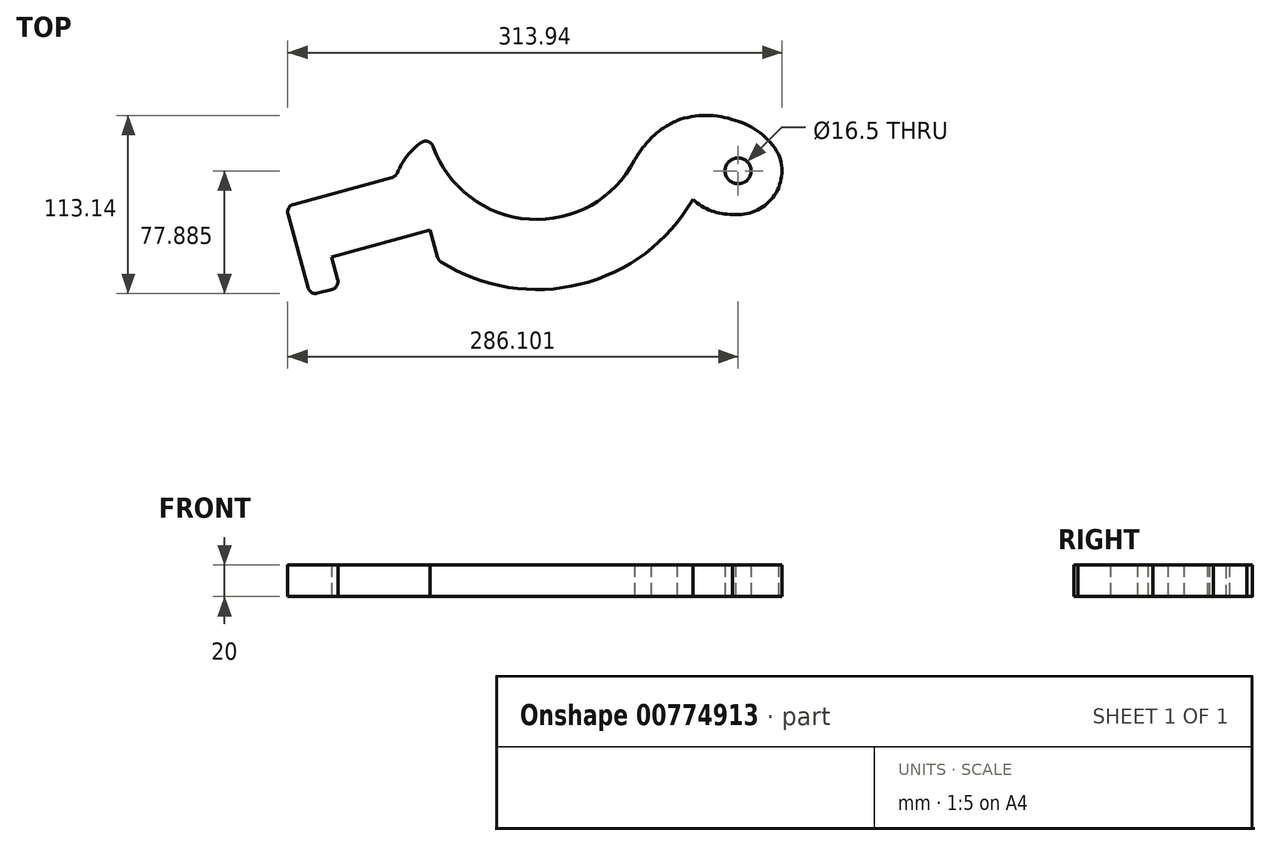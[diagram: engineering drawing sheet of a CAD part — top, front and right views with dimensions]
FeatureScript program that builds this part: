
annotation { "Feature Type Name" : "Feature", "Feature Type Description" : "" }
export const myFeature = defineFeature(function(context is Context, id is Id, definition is map)
    precondition{}
    {
        {
            var Q0;
            Q0=qCreatedBy(makeId("Top.planeOp"),FACE);
            var sketch = newSketch(context, id + "F0", { "sketchPlane" : qUnion([Q0])});
            skArc(sketch, "E0", {"start": v(60.62, -35) * mm, "mid": v(61.37, -33.66) * mm, "end": v(62.1, -32.3) * mm});
            skArc(sketch, "E1", {"start": v(-67.74, -17.64) * mm, "mid": v(-7.86, -69.56) * mm, "end": v(62.1, -32.3) * mm});
            skArc(sketch, "E2.trimOffspring", {"start": v(-67.74, -17.64) * mm, "mid": v(-61.83, -32.8) * mm, "end": v(-52.59, -46.2) * mm});
            skArc(sketch, "E3.trimOffspring", {"start": v(-62.48, -95.92) * mm, "mid": v(26.64, -111.33) * mm, "end": v(99.14, -57.24) * mm});
            skLineSegment(sketch, "E4", {"start": v(0, 0) * mm, "end": v(0, -70) * mm, "construction": true});
            skArc(sketch, "E5", {"start": v(124.4, -66.72) * mm, "mid": v(150.01, -55.92) * mm, "end": v(153.5, -28.33) * mm});
            skCircle(sketch, "E6", {"center": v(127.83, -39.1) * mm, "radius": 8.25 * mm});
            skLineSegment(sketch, "E7", {"start": v(-130.46, -93.7) * mm, "end": v(-67.74, -76.62) * mm});
            skLineSegment(sketch, "E8", {"start": v(-125.2, -113) * mm, "end": v(-130.46, -93.7) * mm});
            skLineSegment(sketch, "E9", {"start": v(0, 0) * mm, "end": v(127.83, -39.1) * mm, "construction": true});
            skLineSegment(sketch, "E10", {"start": v(0, 0) * mm, "end": v(154.45, -47.24) * mm, "construction": true});
            skLineSegment(sketch, "E11", {"start": v(-153.69, -82.63) * mm, "end": v(-144.02, -118.12) * mm});
            skLineSegment(sketch, "E12", {"start": v(-62.48, -95.92) * mm, "end": v(-67.74, -76.62) * mm});
            skLineSegment(sketch, "E13", {"start": v(-67.74, -76.62) * mm, "end": v(-67.74, -76.62) * mm});
            skArc(sketch, "E14", {"start": v(72.58, -18.26) * mm, "mid": v(66.02, -26.21) * mm, "end": v(60.62, -35) * mm});
            skArc(sketch, "E15", {"start": v(89.08, -7.13) * mm, "mid": v(73.45, -17.43) * mm, "end": v(62.1, -32.3) * mm});
            skArc(sketch, "E16.trimOffspring", {"start": v(-62.55, -31.42) * mm, "mid": v(-0.5, -70) * mm, "end": v(62.1, -32.3) * mm, "construction": true});
            skLineSegment(sketch, "E17", {"start": v(-153.69, -82.63) * mm, "end": v(-159.4, -61.64) * mm});
            skLineSegment(sketch, "E18", {"start": v(-125.2, -113) * mm, "end": v(-144.02, -118.12) * mm});
            skLineSegment(sketch, "E19", {"start": v(-159.4, -61.64) * mm, "end": v(-89.46, -42.6) * mm});
            skArc(sketch, "E20", {"start": v(-67.74, -17.64) * mm, "mid": v(-81.03, -28) * mm, "end": v(-89.46, -42.6) * mm});
            skCircle(sketch, "E21", {"center": v(0, 0) * mm, "radius": 70 * mm, "construction": true});
            skArc(sketch, "E22.MirrorCS", {"start": v(102.2, -59.8) * mm, "mid": v(101.55, -59.45) * mm, "end": v(100.9, -59.09) * mm});
            skLineSegment(sketch, "E23", {"start": v(0, 0) * mm, "end": v(0, 88.9) * mm, "construction": true});
            skArc(sketch, "E24", {"start": v(99.14, -57.24) * mm, "mid": v(110.82, -64.52) * mm, "end": v(124.4, -66.72) * mm});
            skArc(sketch, "E25", {"start": v(6.46, 1.5) * mm, "mid": v(7.21, 2.85) * mm, "end": v(7.94, 4.2) * mm});
            skLineSegment(sketch, "E26", {"start": v(-121.9, -40.11) * mm, "end": v(-121.9, -40.11) * mm});
            skArc(sketch, "E27", {"start": v(34.92, 29.38) * mm, "mid": v(34.67, 29.28) * mm, "end": v(34.43, 29.17) * mm});
            skArc(sketch, "E28", {"start": v(70.6, 28.85) * mm, "mid": v(70.6, 28.85) * mm, "end": v(70.6, 28.85) * mm});
            skArc(sketch, "E29", {"start": v(126.08, -7.15) * mm, "mid": v(107.58, -3.84) * mm, "end": v(89.08, -7.13) * mm});
            skArc(sketch, "E30", {"start": v(153.5, -28.33) * mm, "mid": v(141.9, -15) * mm, "end": v(126.08, -7.15) * mm});
            skLineSegment(sketch, "E31", {"start": v(127.83, -39.1) * mm, "end": v(127.83, -30.84) * mm});
            skLineSegment(sketch, "E32", {"start": v(127.83, -39.1) * mm, "end": v(127.83, -47.34) * mm});
            skLineSegment(sketch, "E33", {"start": v(127.83, -39.1) * mm, "end": v(119.58, -39.1) * mm});
            skLineSegment(sketch, "E34", {"start": v(127.83, -39.1) * mm, "end": v(136.08, -39.1) * mm});
            skLineSegment(sketch, "E35", {"start": v(127.83, -39.1) * mm, "end": v(127.83, -47.34) * mm, "construction": true});
            skLineSegment(sketch, "E36", {"start": v(127.83, -128.66) * mm, "end": v(27.83, -128.66) * mm});
            skLineSegment(sketch, "E37", {"start": v(27.83, -128.66) * mm, "end": v(27.83, -118.66) * mm});
            skLineSegment(sketch, "E38", {"start": v(127.83, -128.66) * mm, "end": v(127.83, -118.66) * mm});
            skLineSegment(sketch, "E39.trimOffspring", {"start": v(127.83, -118.66) * mm, "end": v(127.83, -128.66) * mm, "construction": true});
            skLineSegment(sketch, "E40", {"start": v(-130.46, -93.7) * mm, "end": v(127.83, -23.37) * mm, "construction": true});
            skPoint(sketch, "E41.endSnap0", {"position": v(123.7, -39.1) * mm});
            skLineSegment(sketch, "E42", {"start": v(127.83, -39.1) * mm, "end": v(123.84, -24.45) * mm, "construction": true});
            skSolve(sketch);
        }
        {
            var Q0;
            Q0=makeQuery(id+"F0.imprint","IMPRINT",FACE,{"disambiguationData":[TD([[makeQuery(id+"F0.imprint","IMPRINT",EDGE,{"derivedFrom":sQuery(id+"F0.wireOp",EDGE,"E1")}),-1.0]])]});
            extrude(context, id + "F1", {"entities" : qUnion([Q0]), "depth" : 20 * mm, "offsetDistance" : 25 * mm});
        }
        {
            var Q0;
            Q0=makeQuery(id+"F1.opExtrude","SWEPT_EDGE",EDGE,{"disambiguationData":[OSD([sQuery(id+"F0.wireOp",EDGE,"E2.trimOffspring"),sQuery(id+"F0.wireOp",EDGE,"E20")])]});
            var Q1;
            Q1=makeQuery(id+"F1.opExtrude","SWEPT_EDGE",EDGE,{"disambiguationData":[OSD([sQuery(id+"F0.wireOp",EDGE,"E17"),sQuery(id+"F0.wireOp",EDGE,"E19")])]});
            var Q2;
            Q2=makeQuery(id+"F1.opExtrude","SWEPT_EDGE",EDGE,{"disambiguationData":[OSD([sQuery(id+"F0.wireOp",EDGE,"E11"),sQuery(id+"F0.wireOp",EDGE,"E18")])]});
            var Q3;
            Q3=makeQuery(id+"F1.opExtrude","SWEPT_EDGE",EDGE,{"disambiguationData":[OSD([sQuery(id+"F0.wireOp",EDGE,"E8"),sQuery(id+"F0.wireOp",EDGE,"E18")])]});
            var Q4;
            Q4=makeQuery(id+"F1.opExtrude","SWEPT_EDGE",EDGE,{"disambiguationData":[OSD([sQuery(id+"F0.wireOp",EDGE,"E3.trimOffspring"),sQuery(id+"F0.wireOp",EDGE,"E12")])]});
            fillet(context, id + "F2", {"entities" : qUnion([Q0, Q1, Q2, Q3, Q4]), "radius" : 5 * mm, "tangentPropagation" : true, "allowEdgeOverflow" : false});
        }
    });
